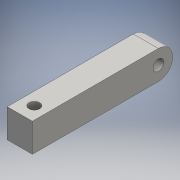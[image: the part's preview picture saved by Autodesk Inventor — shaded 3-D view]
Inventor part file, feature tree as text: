
AUTODESK INVENTOR PART (.ipt)
format: ipt  version: 2016 (Build 200138000, 138)  size: 104,448 bytes
history: native  units: mm
features: sketch x3, hole x2, extrude x1, fillet x1
ambient origin geometry x8: Origin, YZ Plane, XZ Plane, XY Plane, X Axis, Y Axis, Z Axis, Center Point
bodies: Solid1 (feature_tree)
feature tree (7):
  extrude  "Extrusion1"  Depth=7.0mm TaperAngle=0.0deg
  sketch  "Sketch2"  dims[d5=3.0mm d6=6.0mm d7=4.0mm d8=2.0mm d9=90.0deg d10=8.0mm d11=20.594885mm d12=4.0mm]
  fillet  "Fillet2"  Radius=4.0mm
  hole  "Hole1"  [1 undecoded]
  hole  "Hole2"  [1 undecoded]
  sketch  "Sketch1"  dims[d0=8.0mm d1=7.0mm d2=0.0mm d4=4.0mm]
  sketch  "Sketch3"  dims[d13=3.0mm d14=6.0mm d15=4.0mm d16=2.0mm d17=90.0deg d18=8.0mm d19=20.594885mm]
note: 2 required parameter values undecoded (feature->parameter linkage not recoverable at this tier; creation-order binding heuristic only, values carry confidence <= 0.55)
